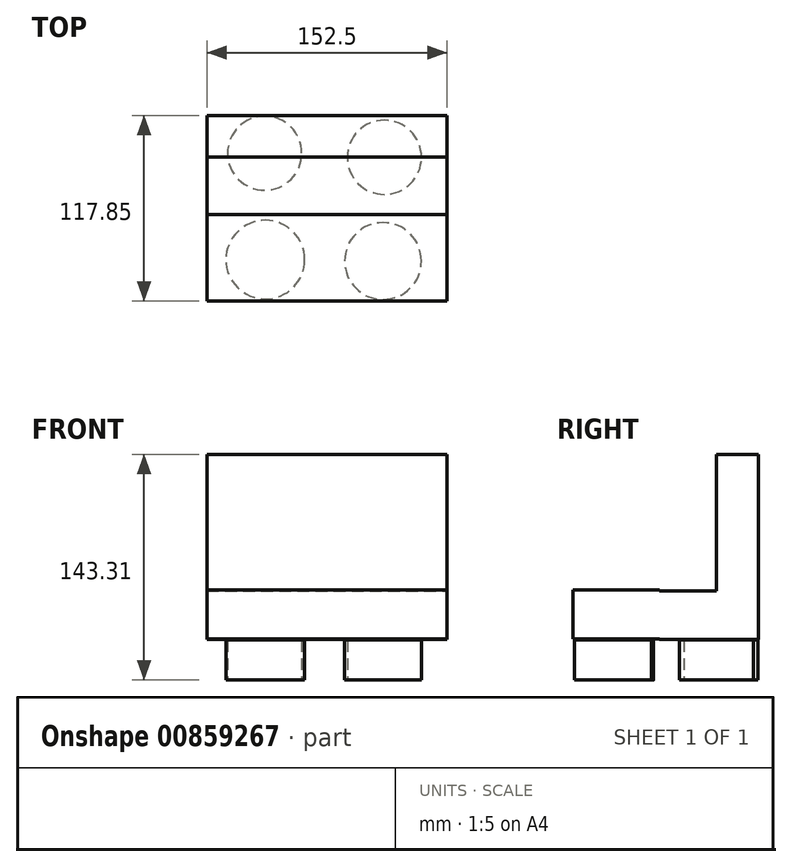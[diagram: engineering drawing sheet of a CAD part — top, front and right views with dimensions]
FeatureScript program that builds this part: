
annotation { "Feature Type Name" : "Feature", "Feature Type Description" : "" }
export const myFeature = defineFeature(function(context is Context, id is Id, definition is map)
    precondition{}
    {
        {
            var Q0;
            Q0=qCreatedBy(makeId("Top.planeOp"),FACE);
            var sketch = newSketch(context, id + "F0", { "sketchPlane" : qUnion([Q0])});
            skCircle(sketch, "E0", {"center": v(-39.67, 39.01) * mm, "radius": 23.54 * mm});
            skCircle(sketch, "E1", {"center": v(36.36, 36.36) * mm, "radius": 23.54 * mm});
            skCircle(sketch, "E2", {"center": v(-39.23, -28.62) * mm, "radius": 25.01 * mm});
            skCircle(sketch, "E3", {"center": v(35.47, -29.5) * mm, "radius": 24.39 * mm});
            skSolve(sketch);
        }
        {
            var Q0;
            Q0=makeQuery(id+"F0.imprint","IMPRINT",FACE,{"disambiguationData":[TD([[makeQuery(id+"F0.imprint","IMPRINT",EDGE,{"derivedFrom":sQuery(id+"F0.wireOp",EDGE,"E0")}),1.0]])]});
            var Q1;
            Q1=makeQuery(id+"F0.imprint","IMPRINT",FACE,{"disambiguationData":[TD([[makeQuery(id+"F0.imprint","IMPRINT",EDGE,{"derivedFrom":sQuery(id+"F0.wireOp",EDGE,"E1")}),1.0]])]});
            var Q2;
            Q2=makeQuery(id+"F0.imprint","IMPRINT",FACE,{"disambiguationData":[TD([[makeQuery(id+"F0.imprint","IMPRINT",EDGE,{"derivedFrom":sQuery(id+"F0.wireOp",EDGE,"E2")}),1.0]])]});
            var Q3;
            Q3=makeQuery(id+"F0.imprint","IMPRINT",FACE,{"disambiguationData":[TD([[makeQuery(id+"F0.imprint","IMPRINT",EDGE,{"derivedFrom":sQuery(id+"F0.wireOp",EDGE,"E3")}),1.0]])]});
            extrude(context, id + "F1", {"entities" : qUnion([Q0, Q1, Q2, Q3]), "depth" : 25.4 * mm, "offsetDistance" : 25.4 * mm});
        }
        {
            var Q0;
            Q0=qCreatedBy(makeId("Front.planeOp"),FACE);
            var sketch = newSketch(context, id + "F2", { "sketchPlane" : qUnion([Q0])});
            skLineSegment(sketch, "E4.bottom", {"start": v(-76.36, 56.7) * mm, "end": v(76.14, 56.7) * mm});
            skLineSegment(sketch, "E4.top", {"start": v(-76.36, 25.75) * mm, "end": v(76.14, 25.75) * mm});
            skLineSegment(sketch, "E4.left", {"start": v(-76.36, 56.7) * mm, "end": v(-76.36, 25.75) * mm});
            skLineSegment(sketch, "E4.right", {"start": v(76.14, 56.7) * mm, "end": v(76.14, 25.75) * mm});
            skSolve(sketch);
        }
        {
            var Q0;
            Q0=makeQuery(id+"F2.imprint","IMPRINT",FACE,{"disambiguationData":[TD([[makeQuery(id+"F2.imprint","IMPRINT",EDGE,{"derivedFrom":sQuery(id+"F2.wireOp",EDGE,"E4.bottom")}),-1.0]])]});
            extrude(context, id + "F3", {"entities" : qUnion([Q0]), "oppositeDirection" : true, "depth" : 63 * mm, "offsetDistance" : 25.4 * mm});
        }
        {
            var Q0;
            Q0=qCreatedBy(makeId("Front.planeOp"),FACE);
            var sketch = newSketch(context, id + "F4", { "sketchPlane" : qUnion([Q0])});
            skLineSegment(sketch, "E5.bottom", {"start": v(-76.36, 57.17) * mm, "end": v(76.14, 57.17) * mm});
            skLineSegment(sketch, "E5.top", {"start": v(-76.36, 26) * mm, "end": v(76.14, 26) * mm});
            skLineSegment(sketch, "E5.left", {"start": v(-76.36, 57.17) * mm, "end": v(-76.36, 26) * mm});
            skLineSegment(sketch, "E5.right", {"start": v(76.14, 57.17) * mm, "end": v(76.14, 26) * mm});
            skSolve(sketch);
        }
        {
            var Q0;
            Q0=makeQuery(id+"F4.imprint","IMPRINT",FACE,{"disambiguationData":[TD([[makeQuery(id+"F4.imprint","IMPRINT",EDGE,{"derivedFrom":sQuery(id+"F4.wireOp",EDGE,"E5.bottom")}),-1.0]])]});
            extrude(context, id + "F5", {"entities" : qUnion([Q0]), "operationType" : NewBodyOperationType.ADD, "depth" : 54.86 * mm, "offsetDistance" : 25.4 * mm});
        }
        {
            var Q0;
            Q0=makeQuery(id+"F3.opExtrude","SWEPT_FACE",FACE,{"disambiguationData":[OSD([sQuery(id+"F2.wireOp",EDGE,"E4.bottom")])]});
            var sketch = newSketch(context, id + "F6", { "sketchPlane" : qUnion([Q0])});
            skLineSegment(sketch, "E6.bottom", {"start": v(-76.36, 63) * mm, "end": v(76.14, 63) * mm});
            skLineSegment(sketch, "E6.top", {"start": v(-76.36, 36.4) * mm, "end": v(76.14, 36.4) * mm});
            skLineSegment(sketch, "E6.left", {"start": v(-76.36, 63) * mm, "end": v(-76.36, 36.4) * mm});
            skLineSegment(sketch, "E6.right", {"start": v(76.14, 63) * mm, "end": v(76.14, 36.4) * mm});
            skSolve(sketch);
        }
        {
            var Q0;
            Q0=makeQuery(id+"F6.imprint","IMPRINT",FACE,{"disambiguationData":[TD([[makeQuery(id+"F6.imprint","IMPRINT",EDGE,{"derivedFrom":sQuery(id+"F6.wireOp",EDGE,"E6.bottom")}),-1.0]])]});
            extrude(context, id + "F7", {"entities" : qUnion([Q0]), "operationType" : NewBodyOperationType.ADD, "depth" : 86.61 * mm, "offsetDistance" : 25.4 * mm});
        }
    });
